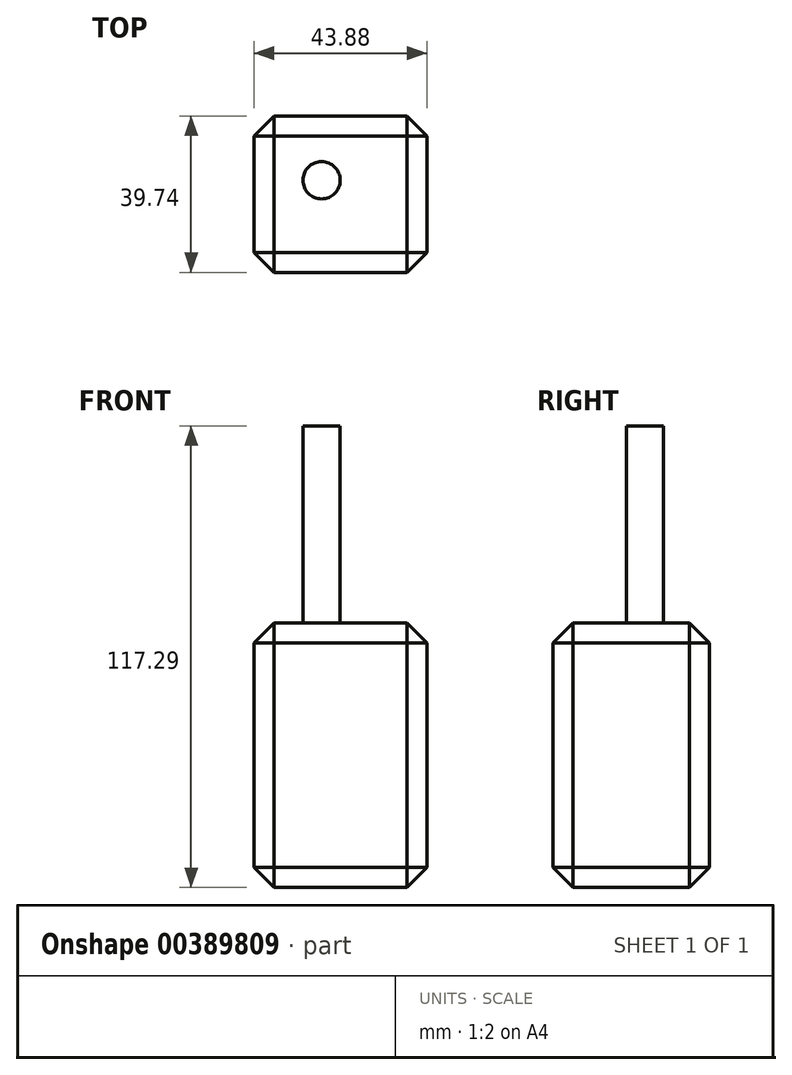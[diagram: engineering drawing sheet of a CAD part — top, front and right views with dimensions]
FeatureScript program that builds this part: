
annotation { "Feature Type Name" : "Feature", "Feature Type Description" : "" }
export const myFeature = defineFeature(function(context is Context, id is Id, definition is map)
    precondition{}
    {
        {
            var Q0;
            Q0=qCreatedBy(makeId("Top.planeOp"),FACE);
            var sketch = newSketch(context, id + "F0", { "sketchPlane" : qUnion([Q0])});
            skLineSegment(sketch, "E0.bottom", {"start": v(-17.12, 0) * mm, "end": v(26.76, 0) * mm});
            skLineSegment(sketch, "E0.top", {"start": v(-17.12, -39.74) * mm, "end": v(26.76, -39.74) * mm});
            skLineSegment(sketch, "E0.left", {"start": v(-17.12, 0) * mm, "end": v(-17.12, -39.74) * mm});
            skLineSegment(sketch, "E0.right", {"start": v(26.76, 0) * mm, "end": v(26.76, -39.74) * mm});
            skSolve(sketch);
        }
        {
            var Q0;
            Q0 = qSketchRegion(id + "F0", true);
            extrude(context, id + "F1", {"entities" : qUnion([Q0]), "depth" : 67.25 * mm});
        }
        {
            var Q0;
            Q0=makeQuery(id+"F1.opExtrude","SWEPT_EDGE",EDGE,{"disambiguationData":[OSD([sQuery(id+"F0.wireOp",EDGE,"E0.top"),sQuery(id+"F0.wireOp",EDGE,"E0.right")])]});
            var Q1;
            Q1=makeQuery(id+"F1.opExtrude","CAP_EDGE",EDGE,{"disambiguationData":[OSD([sQuery(id+"F0.wireOp",EDGE,"E0.right")])],"isStart":false});
            var Q2;
            Q2=makeQuery(id+"F1.opExtrude","CAP_EDGE",EDGE,{"disambiguationData":[OSD([sQuery(id+"F0.wireOp",EDGE,"E0.top")])],"isStart":false});
            var Q3;
            Q3=makeQuery(id+"F1.opExtrude","CAP_EDGE",EDGE,{"disambiguationData":[OSD([sQuery(id+"F0.wireOp",EDGE,"E0.left")])],"isStart":false});
            var Q4;
            Q4=makeQuery(id+"F1.opExtrude","SWEPT_EDGE",EDGE,{"disambiguationData":[OSD([sQuery(id+"F0.wireOp",EDGE,"E0.top"),sQuery(id+"F0.wireOp",EDGE,"E0.left")])]});
            var Q5;
            Q5=makeQuery(id+"F1.opExtrude","CAP_EDGE",EDGE,{"disambiguationData":[OSD([sQuery(id+"F0.wireOp",EDGE,"E0.left")])],"isStart":true});
            var Q6;
            Q6=makeQuery(id+"F1.opExtrude","CAP_EDGE",EDGE,{"disambiguationData":[OSD([sQuery(id+"F0.wireOp",EDGE,"E0.right")])],"isStart":true});
            var Q7;
            Q7=makeQuery(id+"F1.opExtrude","CAP_EDGE",EDGE,{"disambiguationData":[OSD([sQuery(id+"F0.wireOp",EDGE,"E0.bottom")])],"isStart":true});
            var Q8;
            Q8=makeQuery(id+"F1.opExtrude","SWEPT_EDGE",EDGE,{"disambiguationData":[OSD([sQuery(id+"F0.wireOp",EDGE,"E0.bottom"),sQuery(id+"F0.wireOp",EDGE,"E0.right")])]});
            var Q9;
            Q9=makeQuery(id+"F1.opExtrude","SWEPT_EDGE",EDGE,{"disambiguationData":[OSD([sQuery(id+"F0.wireOp",EDGE,"E0.bottom"),sQuery(id+"F0.wireOp",EDGE,"E0.left")])]});
            var Q10;
            Q10=makeQuery(id+"F1.opExtrude","CAP_EDGE",EDGE,{"disambiguationData":[OSD([sQuery(id+"F0.wireOp",EDGE,"E0.bottom")])],"isStart":false});
            var Q11;
            Q11=makeQuery(id+"F1.opExtrude","CAP_EDGE",EDGE,{"disambiguationData":[OSD([sQuery(id+"F0.wireOp",EDGE,"E0.top")])],"isStart":true});
            chamfer(context, id + "F2", {"entities" : qUnion([Q0, Q1, Q2, Q3, Q4, Q5, Q6, Q7, Q8, Q9, Q10, Q11]), "width" : 5.08 * mm, "tangentPropagation" : true});
        }
        {
            var Q0;
            Q0=makeQuery(id+"F1.opExtrude","CAP_FACE",FACE,{"disambiguationData":[OSD([sQuery(id+"F0.wireOp",EDGE,"E0.bottom"),sQuery(id+"F0.wireOp",EDGE,"E0.top"),sQuery(id+"F0.wireOp",EDGE,"E0.left"),sQuery(id+"F0.wireOp",EDGE,"E0.right")])],"isStart":false});
            var sketch = newSketch(context, id + "F3", { "sketchPlane" : qUnion([Q0])});
            skCircle(sketch, "E1", {"center": v(0, -16.33) * mm, "radius": 4.73 * mm});
            skSolve(sketch);
        }
        {
            var Q0;
            Q0 = qSketchRegion(id + "F3", true);
            extrude(context, id + "F4", {"entities" : qUnion([Q0]), "operationType" : NewBodyOperationType.ADD, "depth" : 50.04 * mm});
        }
    });
